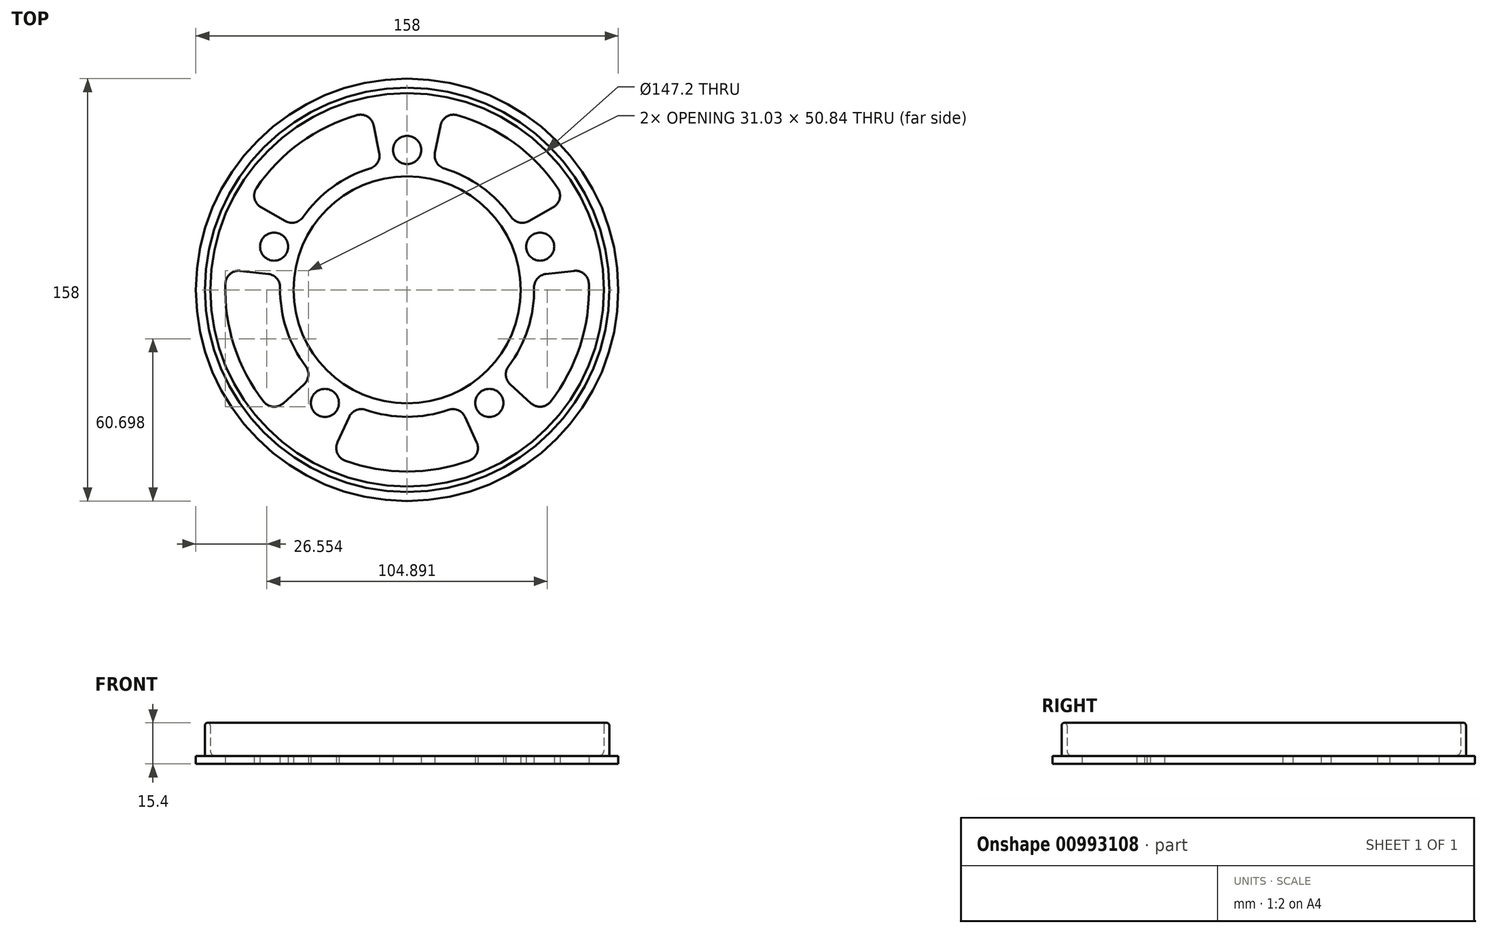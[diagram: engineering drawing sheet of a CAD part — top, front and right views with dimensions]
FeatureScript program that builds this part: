
annotation { "Feature Type Name" : "Feature", "Feature Type Description" : "" }
export const myFeature = defineFeature(function(context is Context, id is Id, definition is map)
    precondition{}
    {
        {
            var Q0;
            Q0=qCreatedBy(makeId("Top.planeOp"),FACE);
            var sketch = newSketch(context, id + "F0", { "sketchPlane" : qUnion([Q0])});
            skCircle(sketch, "E0", {"center": v(0, 0) * mm, "radius": 42.5 * mm});
            skCircle(sketch, "E1", {"center": v(0, 0) * mm, "radius": 68 * mm});
            skCircle(sketch, "E2.cCircle", {"center": v(0, 0) * mm, "radius": 52.32 * mm, "construction": true});
            skLineSegment(sketch, "E2.0", {"start": v(0, 52.32) * mm, "end": v(49.75, 16.17) * mm, "construction": true});
            skLineSegment(sketch, "E2.1", {"start": v(49.75, 16.17) * mm, "end": v(30.75, -42.32) * mm, "construction": true});
            skLineSegment(sketch, "E2.2", {"start": v(30.75, -42.32) * mm, "end": v(-30.75, -42.32) * mm, "construction": true});
            skLineSegment(sketch, "E2.3", {"start": v(-30.75, -42.32) * mm, "end": v(-49.75, 16.17) * mm, "construction": true});
            skLineSegment(sketch, "E2.4", {"start": v(-49.75, 16.17) * mm, "end": v(0, 52.32) * mm, "construction": true});
            skCircle(sketch, "E3", {"center": v(0, 52.32) * mm, "radius": 5.25 * mm});
            skCircle(sketch, "E4", {"center": v(49.75, 16.17) * mm, "radius": 5.25 * mm});
            skCircle(sketch, "E5", {"center": v(30.75, -42.32) * mm, "radius": 5.25 * mm});
            skCircle(sketch, "E6", {"center": v(-30.75, -42.32) * mm, "radius": 5.25 * mm});
            skCircle(sketch, "E7", {"center": v(-49.75, 16.17) * mm, "radius": 5.25 * mm});
            skCircle(sketch, "E8", {"center": v(0, 0) * mm, "radius": 79 * mm});
            skLineSegment(sketch, "E9", {"start": v(0, 0) * mm, "end": v(15.75, 77.41) * mm});
            skLineSegment(sketch, "E10", {"start": v(0, 0) * mm, "end": v(46.44, 63.91) * mm, "construction": true});
            skLineSegment(sketch, "E11.MirrorCS", {"start": v(0, 0) * mm, "end": v(68.76, 38.9) * mm});
            skCircle(sketch, "E12", {"center": v(0, 0) * mm, "radius": 47.5 * mm});
            skLineSegment(sketch, "E13.1.0", {"start": v(0, 0) * mm, "end": v(-68.76, 38.9) * mm});
            skLineSegment(sketch, "E13.1.1", {"start": v(0, 0) * mm, "end": v(-15.75, 77.41) * mm});
            skLineSegment(sketch, "E13.2.0", {"start": v(0, 0) * mm, "end": v(-58.25, -53.37) * mm});
            skLineSegment(sketch, "E13.2.1", {"start": v(0, 0) * mm, "end": v(-78.5, 8.94) * mm});
            skLineSegment(sketch, "E13.3.0", {"start": v(0, 0) * mm, "end": v(32.76, -71.89) * mm});
            skLineSegment(sketch, "E13.3.1", {"start": v(0, 0) * mm, "end": v(-32.76, -71.89) * mm});
            skLineSegment(sketch, "E13.4.0", {"start": v(0, 0) * mm, "end": v(78.5, 8.94) * mm});
            skLineSegment(sketch, "E13.4.1", {"start": v(0, 0) * mm, "end": v(58.25, -53.37) * mm});
            skSolve(sketch);
        }
        {
            var Q0;
            {var subQ0=sQuery(id+"F0.wireOp",EDGE,"E9");var subQ1=sQuery(id+"F0.wireOp",EDGE,"E1");var subQ2=makeQuery(id+"F0.imprint","INTERSECT",VERTEX,{"derivedFrom":[subQ1,subQ0]});Q0=makeQuery(id+"F0.imprint","IMPRINT",FACE,{"disambiguationData":[TD([[makeQuery(id+"F0.imprint","IMPRINT",EDGE,{"disambiguationData":[TD([[subQ2,-1.0]])],"derivedFrom":subQ1}),-1.0]])]});}
            var Q1;
            {var subQ0=sQuery(id+"F0.wireOp",EDGE,"E9");var subQ1=sQuery(id+"F0.wireOp",EDGE,"E1");var subQ2=makeQuery(id+"F0.imprint","INTERSECT",VERTEX,{"derivedFrom":[subQ1,subQ0]});Q1=makeQuery(id+"F0.imprint","IMPRINT",FACE,{"disambiguationData":[TD([[makeQuery(id+"F0.imprint","IMPRINT",EDGE,{"disambiguationData":[TD([[subQ2,1.0]])],"derivedFrom":subQ1}),-1.0]])]});}
            var Q2;
            {var subQ0=sQuery(id+"F0.wireOp",EDGE,"E9");var subQ1=sQuery(id+"F0.wireOp",EDGE,"E0");var subQ2=makeQuery(id+"F0.imprint","INTERSECT",VERTEX,{"derivedFrom":[subQ1,subQ0]});Q2=makeQuery(id+"F0.imprint","IMPRINT",FACE,{"disambiguationData":[TD([[makeQuery(id+"F0.imprint","IMPRINT",EDGE,{"disambiguationData":[TD([[subQ2,1.0]])],"derivedFrom":subQ1}),-1.0]])]});}
            var Q3;
            {var subQ3=sQuery(id+"F0.wireOp",EDGE,"E9");var subQ13=sQuery(id+"F0.wireOp",EDGE,"E0");var subQ20=makeQuery(id+"F0.imprint","INTERSECT",VERTEX,{"derivedFrom":[subQ13,subQ3]});Q3=makeQuery(id+"F0.imprint","IMPRINT",FACE,{"disambiguationData":[TD([[makeQuery(id+"F0.imprint","IMPRINT",EDGE,{"disambiguationData":[TD([[subQ20,-1.0]])],"derivedFrom":subQ13}),-1.0]])]});}
            var Q4;
            {var subQ9=sQuery(id+"F0.wireOp",EDGE,"E1");var subQ16=sQuery(id+"F0.wireOp",EDGE,"E9");var subQ17=makeQuery(id+"F0.imprint","INTERSECT",VERTEX,{"derivedFrom":[subQ9,subQ16]});Q4=makeQuery(id+"F0.imprint","IMPRINT",FACE,{"disambiguationData":[TD([[makeQuery(id+"F0.imprint","IMPRINT",EDGE,{"disambiguationData":[TD([[subQ17,-1.0]])],"derivedFrom":subQ9}),1.0]])]});}
            var Q5;
            {var subQ0=sQuery(id+"F0.wireOp",EDGE,"E11.MirrorCS");var subQ1=sQuery(id+"F0.wireOp",EDGE,"E1");var subQ2=makeQuery(id+"F0.imprint","INTERSECT",VERTEX,{"derivedFrom":[subQ1,subQ0]});Q5=makeQuery(id+"F0.imprint","IMPRINT",FACE,{"disambiguationData":[TD([[makeQuery(id+"F0.imprint","IMPRINT",EDGE,{"disambiguationData":[TD([[subQ2,1.0]])],"derivedFrom":subQ1}),1.0]])]});}
            var Q6;
            {var subQ6=sQuery(id+"F0.wireOp",EDGE,"E11.MirrorCS");var subQ7=sQuery(id+"F0.wireOp",EDGE,"E0");var subQ8=makeQuery(id+"F0.imprint","INTERSECT",VERTEX,{"derivedFrom":[subQ7,subQ6]});Q6=makeQuery(id+"F0.imprint","IMPRINT",FACE,{"disambiguationData":[TD([[makeQuery(id+"F0.imprint","IMPRINT",EDGE,{"disambiguationData":[TD([[subQ8,1.0]])],"derivedFrom":subQ7}),-1.0]])]});}
            var Q7;
            {var subQ0=sQuery(id+"F0.wireOp",EDGE,"E11.MirrorCS");var subQ1=sQuery(id+"F0.wireOp",EDGE,"E1");var subQ2=makeQuery(id+"F0.imprint","INTERSECT",VERTEX,{"derivedFrom":[subQ1,subQ0]});Q7=makeQuery(id+"F0.imprint","IMPRINT",FACE,{"disambiguationData":[TD([[makeQuery(id+"F0.imprint","IMPRINT",EDGE,{"disambiguationData":[TD([[subQ2,1.0]])],"derivedFrom":subQ1}),-1.0]])]});}
            var Q8;
            {var subQ0=sQuery(id+"F0.wireOp",EDGE,"E13.4.0");var subQ1=sQuery(id+"F0.wireOp",EDGE,"E1");var subQ2=makeQuery(id+"F0.imprint","INTERSECT",VERTEX,{"derivedFrom":[subQ1,subQ0]});Q8=makeQuery(id+"F0.imprint","IMPRINT",FACE,{"disambiguationData":[TD([[makeQuery(id+"F0.imprint","IMPRINT",EDGE,{"disambiguationData":[TD([[subQ2,1.0]])],"derivedFrom":subQ1}),-1.0]])]});}
            var Q9;
            {var subQ0=sQuery(id+"F0.wireOp",EDGE,"E13.4.0");var subQ1=sQuery(id+"F0.wireOp",EDGE,"E0");var subQ2=makeQuery(id+"F0.imprint","INTERSECT",VERTEX,{"derivedFrom":[subQ1,subQ0]});Q9=makeQuery(id+"F0.imprint","IMPRINT",FACE,{"disambiguationData":[TD([[makeQuery(id+"F0.imprint","IMPRINT",EDGE,{"disambiguationData":[TD([[subQ2,1.0]])],"derivedFrom":subQ1}),-1.0]])]});}
            var Q10;
            {var subQ6=sQuery(id+"F0.wireOp",EDGE,"E13.3.0");var subQ8=sQuery(id+"F0.wireOp",EDGE,"E0");var subQ10=makeQuery(id+"F0.imprint","INTERSECT",VERTEX,{"derivedFrom":[subQ8,subQ6]});Q10=makeQuery(id+"F0.imprint","IMPRINT",FACE,{"disambiguationData":[TD([[makeQuery(id+"F0.imprint","IMPRINT",EDGE,{"disambiguationData":[TD([[subQ10,-1.0]])],"derivedFrom":subQ8}),-1.0]])]});}
            var Q11;
            {var subQ0=sQuery(id+"F0.wireOp",EDGE,"E13.3.1");var subQ1=sQuery(id+"F0.wireOp",EDGE,"E0");var subQ2=makeQuery(id+"F0.imprint","INTERSECT",VERTEX,{"derivedFrom":[subQ1,subQ0]});Q11=makeQuery(id+"F0.imprint","IMPRINT",FACE,{"disambiguationData":[TD([[makeQuery(id+"F0.imprint","IMPRINT",EDGE,{"disambiguationData":[TD([[subQ2,-1.0]])],"derivedFrom":subQ1}),-1.0]])]});}
            var Q12;
            {var subQ6=sQuery(id+"F0.wireOp",EDGE,"E13.2.0");var subQ8=sQuery(id+"F0.wireOp",EDGE,"E0");var subQ9=makeQuery(id+"F0.imprint","INTERSECT",VERTEX,{"derivedFrom":[subQ8,subQ6]});Q12=makeQuery(id+"F0.imprint","IMPRINT",FACE,{"disambiguationData":[TD([[makeQuery(id+"F0.imprint","IMPRINT",EDGE,{"disambiguationData":[TD([[subQ9,-1.0]])],"derivedFrom":subQ8}),-1.0]])]});}
            var Q13;
            {var subQ0=sQuery(id+"F0.wireOp",EDGE,"E13.2.1");var subQ1=sQuery(id+"F0.wireOp",EDGE,"E0");var subQ2=makeQuery(id+"F0.imprint","INTERSECT",VERTEX,{"derivedFrom":[subQ1,subQ0]});Q13=makeQuery(id+"F0.imprint","IMPRINT",FACE,{"disambiguationData":[TD([[makeQuery(id+"F0.imprint","IMPRINT",EDGE,{"disambiguationData":[TD([[subQ2,-1.0]])],"derivedFrom":subQ1}),-1.0]])]});}
            var Q14;
            {var subQ5=sQuery(id+"F0.wireOp",EDGE,"E13.1.0");var subQ6=sQuery(id+"F0.wireOp",EDGE,"E0");var subQ7=makeQuery(id+"F0.imprint","INTERSECT",VERTEX,{"derivedFrom":[subQ6,subQ5]});Q14=makeQuery(id+"F0.imprint","IMPRINT",FACE,{"disambiguationData":[TD([[makeQuery(id+"F0.imprint","IMPRINT",EDGE,{"disambiguationData":[TD([[subQ7,-1.0]])],"derivedFrom":subQ6}),-1.0]])]});}
            var Q15;
            {var subQ0=sQuery(id+"F0.wireOp",EDGE,"E13.1.1");var subQ1=sQuery(id+"F0.wireOp",EDGE,"E0");var subQ2=makeQuery(id+"F0.imprint","INTERSECT",VERTEX,{"derivedFrom":[subQ1,subQ0]});Q15=makeQuery(id+"F0.imprint","IMPRINT",FACE,{"disambiguationData":[TD([[makeQuery(id+"F0.imprint","IMPRINT",EDGE,{"disambiguationData":[TD([[subQ2,-1.0]])],"derivedFrom":subQ1}),-1.0]])]});}
            var Q16;
            {var subQ3=sQuery(id+"F0.wireOp",EDGE,"E13.1.0");var subQ8=sQuery(id+"F0.wireOp",EDGE,"E1");var subQ9=makeQuery(id+"F0.imprint","INTERSECT",VERTEX,{"derivedFrom":[subQ8,subQ3]});Q16=makeQuery(id+"F0.imprint","IMPRINT",FACE,{"disambiguationData":[TD([[makeQuery(id+"F0.imprint","IMPRINT",EDGE,{"disambiguationData":[TD([[subQ9,-1.0]])],"derivedFrom":subQ8}),1.0]])]});}
            var Q17;
            {var subQ0=sQuery(id+"F0.wireOp",EDGE,"E13.1.0");var subQ1=sQuery(id+"F0.wireOp",EDGE,"E1");var subQ2=makeQuery(id+"F0.imprint","INTERSECT",VERTEX,{"derivedFrom":[subQ1,subQ0]});Q17=makeQuery(id+"F0.imprint","IMPRINT",FACE,{"disambiguationData":[TD([[makeQuery(id+"F0.imprint","IMPRINT",EDGE,{"disambiguationData":[TD([[subQ2,-1.0]])],"derivedFrom":subQ1}),-1.0]])]});}
            var Q18;
            {var subQ0=sQuery(id+"F0.wireOp",EDGE,"E13.2.0");var subQ1=sQuery(id+"F0.wireOp",EDGE,"E1");var subQ2=makeQuery(id+"F0.imprint","INTERSECT",VERTEX,{"derivedFrom":[subQ1,subQ0]});Q18=makeQuery(id+"F0.imprint","IMPRINT",FACE,{"disambiguationData":[TD([[makeQuery(id+"F0.imprint","IMPRINT",EDGE,{"disambiguationData":[TD([[subQ2,-1.0]])],"derivedFrom":subQ1}),-1.0]])]});}
            var Q19;
            {var subQ3=sQuery(id+"F0.wireOp",EDGE,"E13.2.0");var subQ6=sQuery(id+"F0.wireOp",EDGE,"E1");var subQ7=makeQuery(id+"F0.imprint","INTERSECT",VERTEX,{"derivedFrom":[subQ6,subQ3]});Q19=makeQuery(id+"F0.imprint","IMPRINT",FACE,{"disambiguationData":[TD([[makeQuery(id+"F0.imprint","IMPRINT",EDGE,{"disambiguationData":[TD([[subQ7,-1.0]])],"derivedFrom":subQ6}),1.0]])]});}
            var Q20;
            {var subQ0=sQuery(id+"F0.wireOp",EDGE,"E13.2.1");var subQ1=sQuery(id+"F0.wireOp",EDGE,"E1");var subQ2=makeQuery(id+"F0.imprint","INTERSECT",VERTEX,{"derivedFrom":[subQ1,subQ0]});Q20=makeQuery(id+"F0.imprint","IMPRINT",FACE,{"disambiguationData":[TD([[makeQuery(id+"F0.imprint","IMPRINT",EDGE,{"disambiguationData":[TD([[subQ2,-1.0]])],"derivedFrom":subQ1}),-1.0]])]});}
            var Q21;
            {var subQ0=sQuery(id+"F0.wireOp",EDGE,"E13.1.1");var subQ1=sQuery(id+"F0.wireOp",EDGE,"E1");var subQ2=makeQuery(id+"F0.imprint","INTERSECT",VERTEX,{"derivedFrom":[subQ1,subQ0]});Q21=makeQuery(id+"F0.imprint","IMPRINT",FACE,{"disambiguationData":[TD([[makeQuery(id+"F0.imprint","IMPRINT",EDGE,{"disambiguationData":[TD([[subQ2,-1.0]])],"derivedFrom":subQ1}),-1.0]])]});}
            var Q22;
            {var subQ0=sQuery(id+"F0.wireOp",EDGE,"E13.3.1");var subQ1=sQuery(id+"F0.wireOp",EDGE,"E1");var subQ2=makeQuery(id+"F0.imprint","INTERSECT",VERTEX,{"derivedFrom":[subQ1,subQ0]});Q22=makeQuery(id+"F0.imprint","IMPRINT",FACE,{"disambiguationData":[TD([[makeQuery(id+"F0.imprint","IMPRINT",EDGE,{"disambiguationData":[TD([[subQ2,-1.0]])],"derivedFrom":subQ1}),-1.0]])]});}
            var Q23;
            {var subQ0=sQuery(id+"F0.wireOp",EDGE,"E13.3.0");var subQ1=sQuery(id+"F0.wireOp",EDGE,"E1");var subQ2=makeQuery(id+"F0.imprint","INTERSECT",VERTEX,{"derivedFrom":[subQ1,subQ0]});Q23=makeQuery(id+"F0.imprint","IMPRINT",FACE,{"disambiguationData":[TD([[makeQuery(id+"F0.imprint","IMPRINT",EDGE,{"disambiguationData":[TD([[subQ2,-1.0]])],"derivedFrom":subQ1}),-1.0]])]});}
            var Q24;
            {var subQ6=sQuery(id+"F0.wireOp",EDGE,"E13.3.0");var subQ8=sQuery(id+"F0.wireOp",EDGE,"E1");var subQ9=makeQuery(id+"F0.imprint","INTERSECT",VERTEX,{"derivedFrom":[subQ8,subQ6]});Q24=makeQuery(id+"F0.imprint","IMPRINT",FACE,{"disambiguationData":[TD([[makeQuery(id+"F0.imprint","IMPRINT",EDGE,{"disambiguationData":[TD([[subQ9,-1.0]])],"derivedFrom":subQ8}),1.0]])]});}
            extrude(context, id + "F1", {"entities" : qUnion([Q0, Q1, Q2, Q3, Q4, Q5, Q6, Q7, Q8, Q9, Q10, Q11, Q12, Q13, Q14, Q15, Q16, Q17, Q18, Q19, Q20, Q21, Q22, Q23, Q24]), "depth" : 3 * mm, "offsetDistance" : 25 * mm});
        }
        {
            var Q0;
            Q0=makeQuery(id+"F1.opExtrude","SWEPT_EDGE",EDGE,{"disambiguationData":[OSD([sQuery(id+"F0.wireOp",EDGE,"E1"),sQuery(id+"F0.wireOp",EDGE,"E9")])]});
            var Q1;
            Q1=makeQuery(id+"F1.opExtrude","SWEPT_EDGE",EDGE,{"disambiguationData":[OSD([sQuery(id+"F0.wireOp",EDGE,"E1"),sQuery(id+"F0.wireOp",EDGE,"E11.MirrorCS")])]});
            var Q2;
            Q2=makeQuery(id+"F1.opExtrude","SWEPT_EDGE",EDGE,{"disambiguationData":[OSD([sQuery(id+"F0.wireOp",EDGE,"E11.MirrorCS"),sQuery(id+"F0.wireOp",EDGE,"E12")])]});
            var Q3;
            Q3=makeQuery(id+"F1.opExtrude","SWEPT_EDGE",EDGE,{"disambiguationData":[OSD([sQuery(id+"F0.wireOp",EDGE,"E9"),sQuery(id+"F0.wireOp",EDGE,"E12")])]});
            var Q4;
            Q4=makeQuery(id+"F1.opExtrude","SWEPT_EDGE",EDGE,{"disambiguationData":[OSD([sQuery(id+"F0.wireOp",EDGE,"E12"),sQuery(id+"F0.wireOp",EDGE,"E13.4.1")])]});
            var Q5;
            Q5=makeQuery(id+"F1.opExtrude","SWEPT_EDGE",EDGE,{"disambiguationData":[OSD([sQuery(id+"F0.wireOp",EDGE,"E12"),sQuery(id+"F0.wireOp",EDGE,"E13.4.0")])]});
            var Q6;
            Q6=makeQuery(id+"F1.opExtrude","SWEPT_EDGE",EDGE,{"disambiguationData":[OSD([sQuery(id+"F0.wireOp",EDGE,"E1"),sQuery(id+"F0.wireOp",EDGE,"E13.4.0")])]});
            var Q7;
            Q7=makeQuery(id+"F1.opExtrude","SWEPT_EDGE",EDGE,{"disambiguationData":[OSD([sQuery(id+"F0.wireOp",EDGE,"E1"),sQuery(id+"F0.wireOp",EDGE,"E13.1.1")])]});
            var Q8;
            Q8=makeQuery(id+"F1.opExtrude","SWEPT_EDGE",EDGE,{"disambiguationData":[OSD([sQuery(id+"F0.wireOp",EDGE,"E1"),sQuery(id+"F0.wireOp",EDGE,"E13.4.1")])]});
            var Q9;
            Q9=makeQuery(id+"F1.opExtrude","SWEPT_EDGE",EDGE,{"disambiguationData":[OSD([sQuery(id+"F0.wireOp",EDGE,"E1"),sQuery(id+"F0.wireOp",EDGE,"E13.3.0")])]});
            var Q10;
            Q10=makeQuery(id+"F1.opExtrude","SWEPT_EDGE",EDGE,{"disambiguationData":[OSD([sQuery(id+"F0.wireOp",EDGE,"E12"),sQuery(id+"F0.wireOp",EDGE,"E13.3.0")])]});
            var Q11;
            Q11=makeQuery(id+"F1.opExtrude","SWEPT_EDGE",EDGE,{"disambiguationData":[OSD([sQuery(id+"F0.wireOp",EDGE,"E12"),sQuery(id+"F0.wireOp",EDGE,"E13.2.1")])]});
            var Q12;
            Q12=makeQuery(id+"F1.opExtrude","SWEPT_EDGE",EDGE,{"disambiguationData":[OSD([sQuery(id+"F0.wireOp",EDGE,"E12"),sQuery(id+"F0.wireOp",EDGE,"E13.2.0")])]});
            var Q13;
            Q13=makeQuery(id+"F1.opExtrude","SWEPT_EDGE",EDGE,{"disambiguationData":[OSD([sQuery(id+"F0.wireOp",EDGE,"E12"),sQuery(id+"F0.wireOp",EDGE,"E13.3.1")])]});
            var Q14;
            Q14=makeQuery(id+"F1.opExtrude","SWEPT_EDGE",EDGE,{"disambiguationData":[OSD([sQuery(id+"F0.wireOp",EDGE,"E1"),sQuery(id+"F0.wireOp",EDGE,"E13.3.1")])]});
            var Q15;
            Q15=makeQuery(id+"F1.opExtrude","SWEPT_EDGE",EDGE,{"disambiguationData":[OSD([sQuery(id+"F0.wireOp",EDGE,"E1"),sQuery(id+"F0.wireOp",EDGE,"E13.2.0")])]});
            var Q16;
            Q16=makeQuery(id+"F1.opExtrude","SWEPT_EDGE",EDGE,{"disambiguationData":[OSD([sQuery(id+"F0.wireOp",EDGE,"E1"),sQuery(id+"F0.wireOp",EDGE,"E13.2.1")])]});
            var Q17;
            Q17=makeQuery(id+"F1.opExtrude","SWEPT_EDGE",EDGE,{"disambiguationData":[OSD([sQuery(id+"F0.wireOp",EDGE,"E1"),sQuery(id+"F0.wireOp",EDGE,"E13.1.0")])]});
            var Q18;
            Q18=makeQuery(id+"F1.opExtrude","SWEPT_EDGE",EDGE,{"disambiguationData":[OSD([sQuery(id+"F0.wireOp",EDGE,"E12"),sQuery(id+"F0.wireOp",EDGE,"E13.1.0")])]});
            var Q19;
            Q19=makeQuery(id+"F1.opExtrude","SWEPT_EDGE",EDGE,{"disambiguationData":[OSD([sQuery(id+"F0.wireOp",EDGE,"E12"),sQuery(id+"F0.wireOp",EDGE,"E13.1.1")])]});
            fillet(context, id + "F2", {"entities" : qUnion([Q0, Q1, Q2, Q3, Q4, Q5, Q6, Q7, Q8, Q9, Q10, Q11, Q12, Q13, Q14, Q15, Q16, Q17, Q18, Q19]), "radius" : 5 * mm, "tangentPropagation" : true, "allowEdgeOverflow" : false});
        }
        {
            var Q0;
            Q0=makeQuery(id+"F1.opExtrude","CAP_FACE",FACE,{"disambiguationData":[OSD([sQuery(id+"F0.wireOp",EDGE,"E0"),sQuery(id+"F0.wireOp",EDGE,"E1"),sQuery(id+"F0.wireOp",EDGE,"E3"),sQuery(id+"F0.wireOp",EDGE,"E4"),sQuery(id+"F0.wireOp",EDGE,"E5"),sQuery(id+"F0.wireOp",EDGE,"E6"),sQuery(id+"F0.wireOp",EDGE,"E7"),sQuery(id+"F0.wireOp",EDGE,"E8"),sQuery(id+"F0.wireOp",EDGE,"E9"),sQuery(id+"F0.wireOp",EDGE,"E11.MirrorCS"),sQuery(id+"F0.wireOp",EDGE,"E12"),sQuery(id+"F0.wireOp",EDGE,"E13.1.0"),sQuery(id+"F0.wireOp",EDGE,"E13.1.1"),sQuery(id+"F0.wireOp",EDGE,"E13.2.0"),sQuery(id+"F0.wireOp",EDGE,"E13.2.1"),sQuery(id+"F0.wireOp",EDGE,"E13.3.0"),sQuery(id+"F0.wireOp",EDGE,"E13.3.1"),sQuery(id+"F0.wireOp",EDGE,"E13.4.0"),sQuery(id+"F0.wireOp",EDGE,"E13.4.1")])],"isStart":false});
            var sketch = newSketch(context, id + "F3", { "sketchPlane" : qUnion([Q0])});
            skCircle(sketch, "E14", {"center": v(0, 0) * mm, "radius": 75.6 * mm});
            skCircle(sketch, "E15.0", {"center": v(0, 0) * mm, "radius": 73.6 * mm});
            skSolve(sketch);
        }
        {
            var Q0;
            Q0 = qSketchRegion(id + "F3", true);
            extrude(context, id + "F4", {"entities" : qUnion([Q0]), "operationType" : NewBodyOperationType.ADD, "depth" : 12.4 * mm, "offsetDistance" : 25 * mm});
        }
        {
            var Q0;
            Q0=makeQuery(id+"F4.opExtrude","CAP_FACE",FACE,{"disambiguationData":[OSD([sQuery(id+"F3.wireOp",EDGE,"E14"),sQuery(id+"F3.wireOp",EDGE,"E15.0")])],"isStart":false});
            fillet(context, id + "F5", {"entities" : qUnion([Q0]), "radius" : 1 * mm, "tangentPropagation" : true, "allowEdgeOverflow" : false});
        }
        {
            var Q0;
            Q0=makeQuery(id+"F4.opExtrude","CAP_EDGE",EDGE,{"disambiguationData":[OSD([sQuery(id+"F3.wireOp",EDGE,"E15.0")])],"isStart":true});
            fillet(context, id + "F6", {"entities" : qUnion([Q0]), "radius" : 2 * mm, "tangentPropagation" : true, "allowEdgeOverflow" : false});
        }
    });
